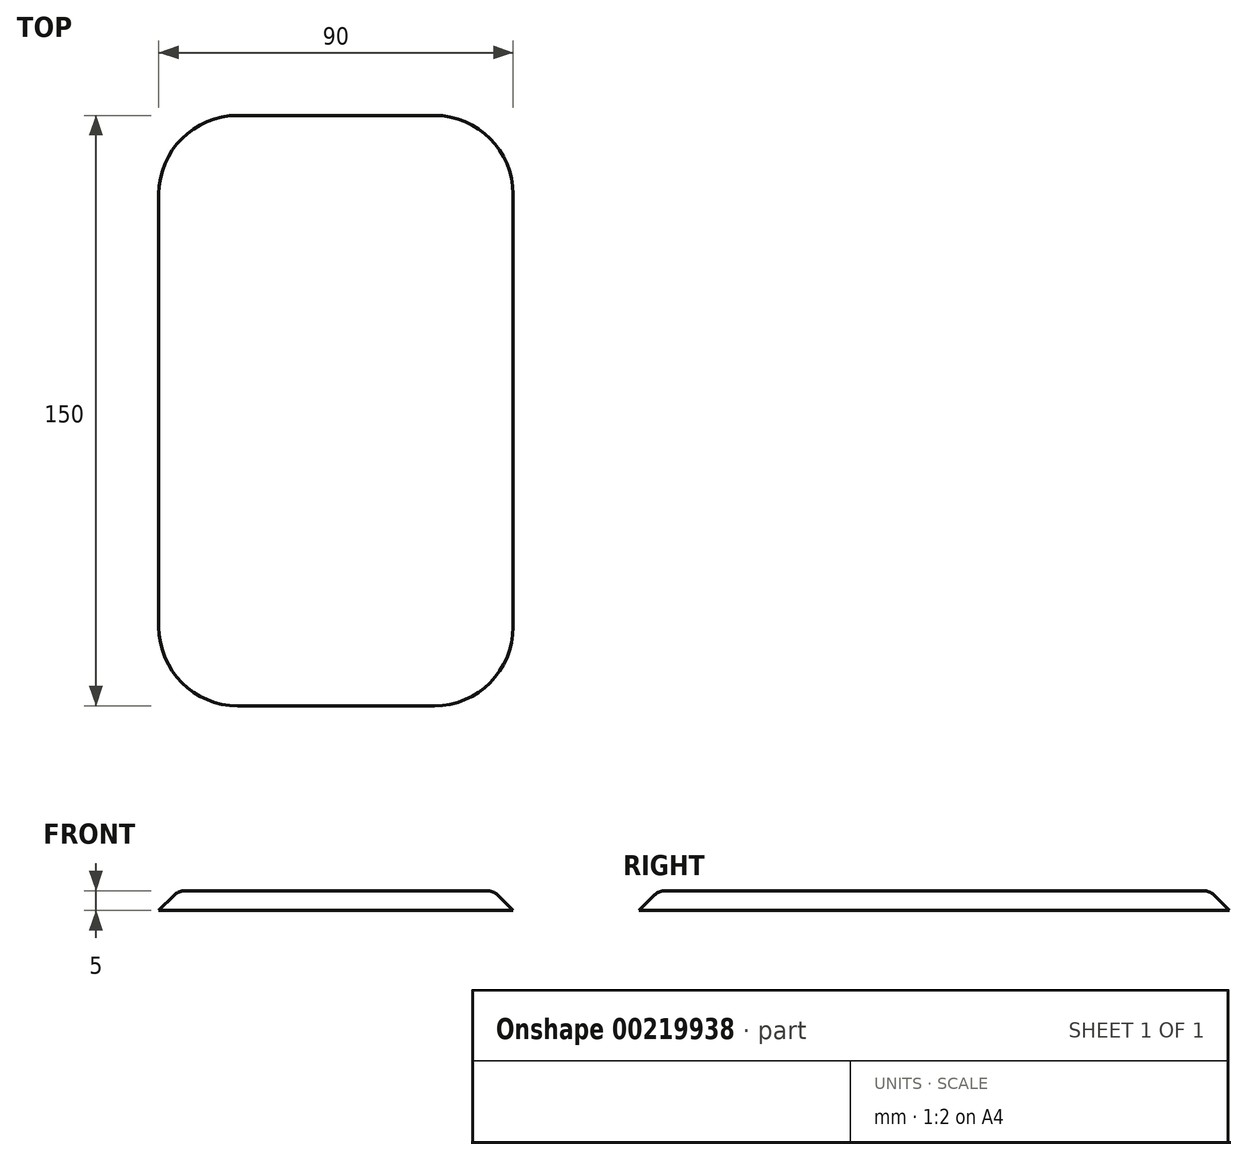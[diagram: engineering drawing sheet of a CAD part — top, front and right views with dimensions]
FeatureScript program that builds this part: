
annotation { "Feature Type Name" : "Feature", "Feature Type Description" : "" }
export const myFeature = defineFeature(function(context is Context, id is Id, definition is map)
    precondition{}
    {
        {
            var Q0;
            Q0=qCreatedBy(makeId("Top.planeOp"),FACE);
            var sketch = newSketch(context, id + "F0", { "sketchPlane" : qUnion([Q0])});
            skLineSegment(sketch, "E0.bottom", {"start": v(-25, 75) * mm, "end": v(25, 75) * mm});
            skLineSegment(sketch, "E0.top", {"start": v(-25, -75) * mm, "end": v(25, -75) * mm});
            skLineSegment(sketch, "E0.left", {"start": v(-45, 55) * mm, "end": v(-45, -55) * mm});
            skLineSegment(sketch, "E0.right", {"start": v(45, 55) * mm, "end": v(45, -55) * mm});
            skPoint(sketch, "E1", {"position": v(0, 75) * mm});
            skPoint(sketch, "E2", {"position": v(-45, 0) * mm});
            skPoint(sketch, "E3.visualSharp", {"position": v(-45, 75) * mm});
            skArc(sketch, "E3.filletArc", {"start": v(-25, 75) * mm, "mid": v(-39.14, 69.14) * mm, "end": v(-45, 55) * mm});
            skPoint(sketch, "E4.visualSharp", {"position": v(45, 75) * mm});
            skArc(sketch, "E4.filletArc", {"start": v(45, 55) * mm, "mid": v(39.14, 69.14) * mm, "end": v(25, 75) * mm});
            skPoint(sketch, "E5.visualSharp", {"position": v(-45, -75) * mm});
            skArc(sketch, "E5.filletArc", {"start": v(-45, -55) * mm, "mid": v(-39.14, -69.14) * mm, "end": v(-25, -75) * mm});
            skPoint(sketch, "E6.visualSharp", {"position": v(45, -75) * mm});
            skArc(sketch, "E6.filletArc", {"start": v(25, -75) * mm, "mid": v(39.14, -69.14) * mm, "end": v(45, -55) * mm});
            skSolve(sketch);
        }
        {
            var Q0;
            Q0=makeQuery(id+"F0.imprint","IMPRINT",FACE,{"disambiguationData":[TD([[makeQuery(id+"F0.imprint","IMPRINT",EDGE,{"derivedFrom":sQuery(id+"F0.wireOp",EDGE,"E0.bottom")}),-1.0]])]});
            extrude(context, id + "F1", {"entities" : qUnion([Q0]), "depth" : 5 * mm});
        }
        {
            var Q0;
            Q0=makeQuery(id+"F1.opExtrude","CAP_EDGE",EDGE,{"disambiguationData":[OSD([sQuery(id+"F0.wireOp",EDGE,"E5.filletArc")])],"isStart":false});
            var Q1;
            Q1=makeQuery(id+"F1.opExtrude","CAP_EDGE",EDGE,{"disambiguationData":[OSD([sQuery(id+"F0.wireOp",EDGE,"E0.top")])],"isStart":false});
            var Q2;
            Q2=makeQuery(id+"F1.opExtrude","CAP_EDGE",EDGE,{"disambiguationData":[OSD([sQuery(id+"F0.wireOp",EDGE,"E6.filletArc")])],"isStart":false});
            var Q3;
            Q3=makeQuery(id+"F1.opExtrude","CAP_EDGE",EDGE,{"disambiguationData":[OSD([sQuery(id+"F0.wireOp",EDGE,"E0.right")])],"isStart":false});
            var Q4;
            Q4=makeQuery(id+"F1.opExtrude","CAP_EDGE",EDGE,{"disambiguationData":[OSD([sQuery(id+"F0.wireOp",EDGE,"E4.filletArc")])],"isStart":false});
            var Q5;
            Q5=makeQuery(id+"F1.opExtrude","CAP_EDGE",EDGE,{"disambiguationData":[OSD([sQuery(id+"F0.wireOp",EDGE,"E0.bottom")])],"isStart":false});
            var Q6;
            Q6=makeQuery(id+"F1.opExtrude","CAP_EDGE",EDGE,{"disambiguationData":[OSD([sQuery(id+"F0.wireOp",EDGE,"E3.filletArc")])],"isStart":false});
            var Q7;
            Q7=makeQuery(id+"F1.opExtrude","CAP_EDGE",EDGE,{"disambiguationData":[OSD([sQuery(id+"F0.wireOp",EDGE,"E0.left")])],"isStart":false});
            chamfer(context, id + "F2", {"entities" : qUnion([Q0, Q1, Q2, Q3, Q4, Q5, Q6, Q7]), "width" : 5 * mm, "tangentPropagation" : true});
        }
        {
            var Q0;
            Q0=makeQuery(id+"F1.opExtrude","CAP_FACE",FACE,{"disambiguationData":[OSD([sQuery(id+"F0.wireOp",EDGE,"E0.bottom"),sQuery(id+"F0.wireOp",EDGE,"E0.top"),sQuery(id+"F0.wireOp",EDGE,"E0.left"),sQuery(id+"F0.wireOp",EDGE,"E0.right"),sQuery(id+"F0.wireOp",EDGE,"E3.filletArc"),sQuery(id+"F0.wireOp",EDGE,"E4.filletArc"),sQuery(id+"F0.wireOp",EDGE,"E5.filletArc"),sQuery(id+"F0.wireOp",EDGE,"E6.filletArc")])],"isStart":false});
            fillet(context, id + "F3", {"entities" : qUnion([Q0]), "radius" : 4 * mm, "tangentPropagation" : true, "allowEdgeOverflow" : false});
        }
        {
            var Q0;
            Q0=makeQuery(id+"F1.opExtrude","CAP_FACE",FACE,{"disambiguationData":[OSD([sQuery(id+"F0.wireOp",EDGE,"E0.bottom"),sQuery(id+"F0.wireOp",EDGE,"E0.top"),sQuery(id+"F0.wireOp",EDGE,"E0.left"),sQuery(id+"F0.wireOp",EDGE,"E0.right"),sQuery(id+"F0.wireOp",EDGE,"E3.filletArc"),sQuery(id+"F0.wireOp",EDGE,"E4.filletArc"),sQuery(id+"F0.wireOp",EDGE,"E5.filletArc"),sQuery(id+"F0.wireOp",EDGE,"E6.filletArc")])],"isStart":false});
            var sketch = newSketch(context, id + "F4", { "sketchPlane" : qUnion([Q0])});
            skLineSegment(sketch, "E7.bottom", {"start": v(-18.5, 40) * mm, "end": v(-8.5, 40) * mm});
            skLineSegment(sketch, "E7.top", {"start": v(-18.5, -38) * mm, "end": v(-8.5, -38) * mm});
            skLineSegment(sketch, "E7.left", {"start": v(-18.5, 40) * mm, "end": v(-18.5, -38) * mm});
            skLineSegment(sketch, "E7.right", {"start": v(-8.5, 40) * mm, "end": v(-8.5, -38) * mm});
            skLineSegment(sketch, "E8.bottom", {"start": v(8.5, 40) * mm, "end": v(18.5, 40) * mm});
            skLineSegment(sketch, "E8.top", {"start": v(8.5, -38) * mm, "end": v(18.5, -38) * mm});
            skLineSegment(sketch, "E8.left", {"start": v(8.5, 40) * mm, "end": v(8.5, -38) * mm});
            skLineSegment(sketch, "E8.right", {"start": v(18.5, 40) * mm, "end": v(18.5, -38) * mm});
            skSolve(sketch);
        }
        {
            var Q0;
            Q0=makeQuery(id+"F4.imprint","IMPRINT",FACE,{"disambiguationData":[TD([[makeQuery(id+"F4.imprint","IMPRINT",EDGE,{"derivedFrom":sQuery(id+"F4.wireOp",EDGE,"E7.bottom")}),1.0]])]});
            cPlane(context, id + "F5", {"entities" : qUnion([Q0]), "cplaneType" : CPlaneType.OFFSET, "offset" : 50 * mm, "width" : 150 * mm, "height" : 150 * mm});
        }
    });
